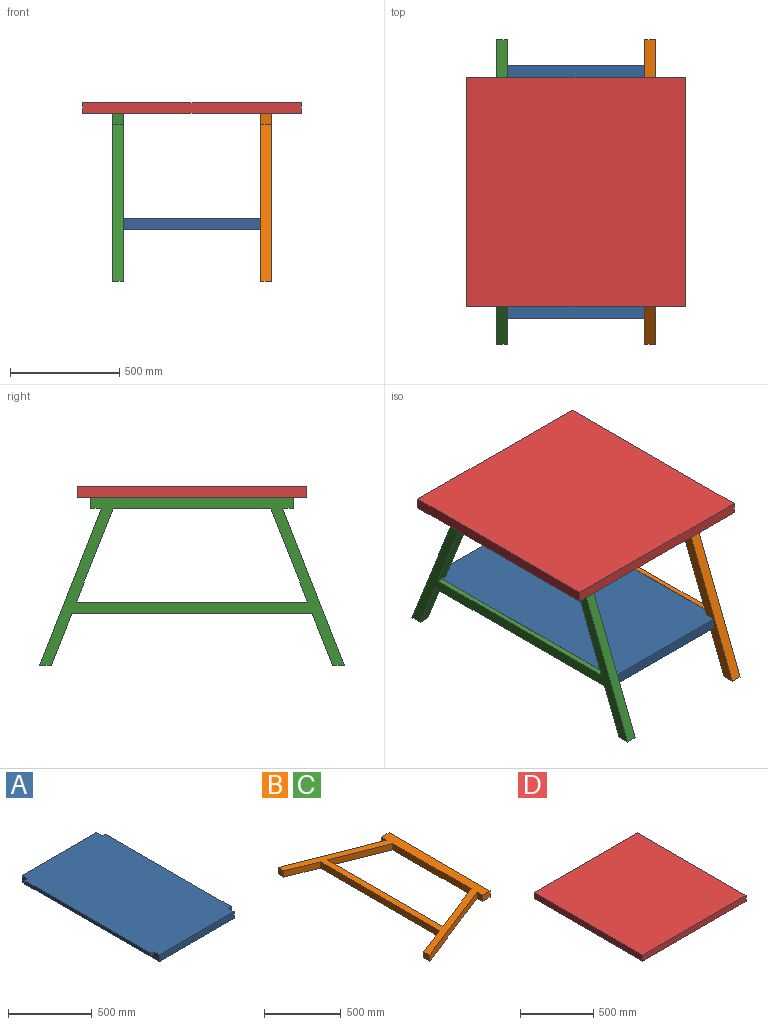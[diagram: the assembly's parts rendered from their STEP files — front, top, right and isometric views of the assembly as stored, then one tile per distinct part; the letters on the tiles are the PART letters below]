
ASSEMBLY  parts=4 mates=3
PART A: 14 faces, bbox 680x1160x50 mm
  f0: plane 1160x630mm, normal (0,0,-1), area 730800mm2, adj f2,f4,f7,f11
  f1: plane 1060x25mm, normal (-1,0,0), area 26500mm2, adj f5,f9,f10,f12
  f2: plane 630x50mm, normal (0,-1,0), area 31500mm2, adj f0,f5,f7,f11
  f3: plane 1060x25mm, normal (1,0,0), area 26500mm2, adj f5,f6,f8,f13
  f4: plane 630x50mm, normal (0,1,0), area 31500mm2, adj f0,f5,f7,f11
  f5: plane 1160x680mm, normal (0,0,1), area 783800mm2, adj f1,f2,f3,f4,f6,f7,f8,f9
  f6: plane 25x25mm, normal (0,-1,0), area 625mm2, adj f3,f5,f7,f13
  f7: plane 1160x50mm, normal (1,0,0), area 31500mm2, adj f0,f2,f4,f5,f6,f8,f13
  f8: plane 25x25mm, normal (0,1,0), area 625mm2, adj f3,f5,f7,f13
  f9: plane 25x25mm, normal (0,1,0), area 625mm2, adj f1,f5,f11,f12
  f10: plane 25x25mm, normal (0,-1,0), area 625mm2, adj f1,f5,f11,f12
  f11: plane 1160x50mm, normal (-1,0,0), area 31500mm2, adj f0,f2,f4,f5,f9,f10,f12
  f12: plane 1060x25mm, normal (0,0,-1), area 26500mm2, adj f1,f9,f10,f11
  f13: plane 1060x25mm, normal (0,0,-1), area 26500mm2, adj f3,f6,f7,f8
PART B: 22 faces, bbox 790x1397.5x50 mm
  f0: plane 1397.49x790mm, normal (0,0,-1), area 170010.2mm2, adj f1,f2,f3,f4,f5,f6,f7,f8
  f1: plane 50x50mm, normal (-1,0,0), area 2500mm2, adj f0,f2,f16,f17
  f2: plane 720x283.74mm, normal (0.37,0.93,0), area 38694.6mm2, adj f0,f1,f3,f17
  f3: plane 53.74x50mm, normal (-1,0,0), area 2687.1mm2, adj f0,f2,f4,f17
  f4: plane 240x94.58mm, normal (-0.37,-0.93,0), area 12898.2mm2, adj f0,f3,f5,f17
  f5: plane 1100.84x50mm, normal (-1,0,0), area 55041.9mm2, adj f0,f4,f6,f17
  f6: plane 240x94.58mm, normal (-0.37,0.93,0), area 12898.2mm2, adj f0,f5,f7,f17
  f7: plane 53.74x50mm, normal (-1,0,0), area 2687.1mm2, adj f0,f6,f8,f17
  f8: plane 720x283.74mm, normal (0.37,-0.93,0), area 38694.6mm2, adj f0,f7,f9,f17
  f9: plane 50x50mm, normal (-1,0,0), area 2500mm2, adj f0,f8,f10,f17
  f10: plane 70x50mm, normal (0,-1,0), area 3500mm2, adj f0,f9,f11,f17
  f11: plane 930x50mm, normal (1,0,0), area 46500mm2, adj f0,f10,f16,f17
  f12: plane 722.52x50mm, normal (-1,0,0), area 36125.7mm2, adj f0,f13,f15,f17
  f13: plane 430x169.46mm, normal (-0.37,0.93,0), area 23109.3mm2, adj f0,f12,f14,f17,f18
  f14: plane 1061.43x25mm, normal (1,0,0), area 26535.7mm2, adj f13,f15,f17,f21
  f15: plane 430x169.46mm, normal (-0.37,-0.93,0), area 23109.3mm2, adj f0,f12,f14,f17,f20
  f16: plane 70x50mm, normal (0,1,0), area 3500mm2, adj f0,f1,f11,f17
  f17: plane 1397.49x790mm, normal (0,0,1), area 196546mm2, adj f1,f2,f3,f4,f5,f6,f7,f8
  f18: plane 25x25mm, normal (0,1,0), area 625mm2, adj f0,f13,f19,f21
  f19: plane 1061.43x25mm, normal (1,0,0), area 26535.7mm2, adj f0,f18,f20,f21
  f20: plane 25x25mm, normal (0,-1,0), area 625mm2, adj f0,f15,f19,f21
  f21: plane 1061.43x25mm, normal (0,0,-1), area 26535.7mm2, adj f14,f18,f19,f20
PART C: same geometry as B
PART D: 16 faces, bbox 1000x1050x50 mm
  f0: plane 1050x1000mm, normal (0,0,-1), area 957000mm2, adj f1,f2,f3,f4,f6,f7,f8,f9
  f1: plane 1050x50mm, normal (1,0,0), area 52500mm2, adj f0,f2,f4,f5
  f2: plane 1000x50mm, normal (0,1,0), area 50000mm2, adj f0,f1,f3,f5
  f3: plane 1050x50mm, normal (-1,0,0), area 52500mm2, adj f0,f2,f4,f5
  f4: plane 1000x50mm, normal (0,-1,0), area 50000mm2, adj f0,f1,f3,f5
  f5: plane 1050x1000mm, normal (0,0,1), area 1050000mm2, adj f1,f2,f3,f4
  f6: plane 50x20mm, normal (0,1,0), area 1000mm2, adj f0,f7,f9,f10
  f7: plane 930x20mm, normal (1,0,0), area 18600mm2, adj f0,f6,f8,f10
  f8: plane 50x20mm, normal (0,-1,0), area 1000mm2, adj f0,f7,f9,f10
  f9: plane 930x20mm, normal (-1,0,0), area 18600mm2, adj f0,f6,f8,f10
  f10: plane 930x50mm, normal (0,0,-1), area 46500mm2, adj f6,f7,f8,f9
  f11: plane 50x20mm, normal (0,1,0), area 1000mm2, adj f0,f12,f14,f15
  f12: plane 930x20mm, normal (1,0,0), area 18600mm2, adj f0,f11,f13,f15
  f13: plane 50x20mm, normal (0,-1,0), area 1000mm2, adj f0,f12,f14,f15
  f14: plane 930x20mm, normal (-1,0,0), area 18600mm2, adj f0,f11,f13,f15
  f15: plane 930x50mm, normal (0,0,-1), area 46500mm2, adj f11,f12,f13,f14
PLACE A t=(1966.75,-99.65,-530)mm
PLACE B rot(axis=(0.71,0,0.71),180deg) t=(315,133.76,547.32)mm
PLACE C rot(axis=(0,-1,0),90deg) t=(-315,-133.76,547.32)mm
PLACE D at identity fixed
MATE fastened B.f11 <-> D.f10  axis (0,0,1) through (315,-465,20)mm
MATE fastened D.f15 <-> C.f11  axis (0,0,-1) through (-315,-465,20)mm
MATE fastened A.f3 <-> B.f21  axis (1,0,0) through (340,530.71,-480)mm
